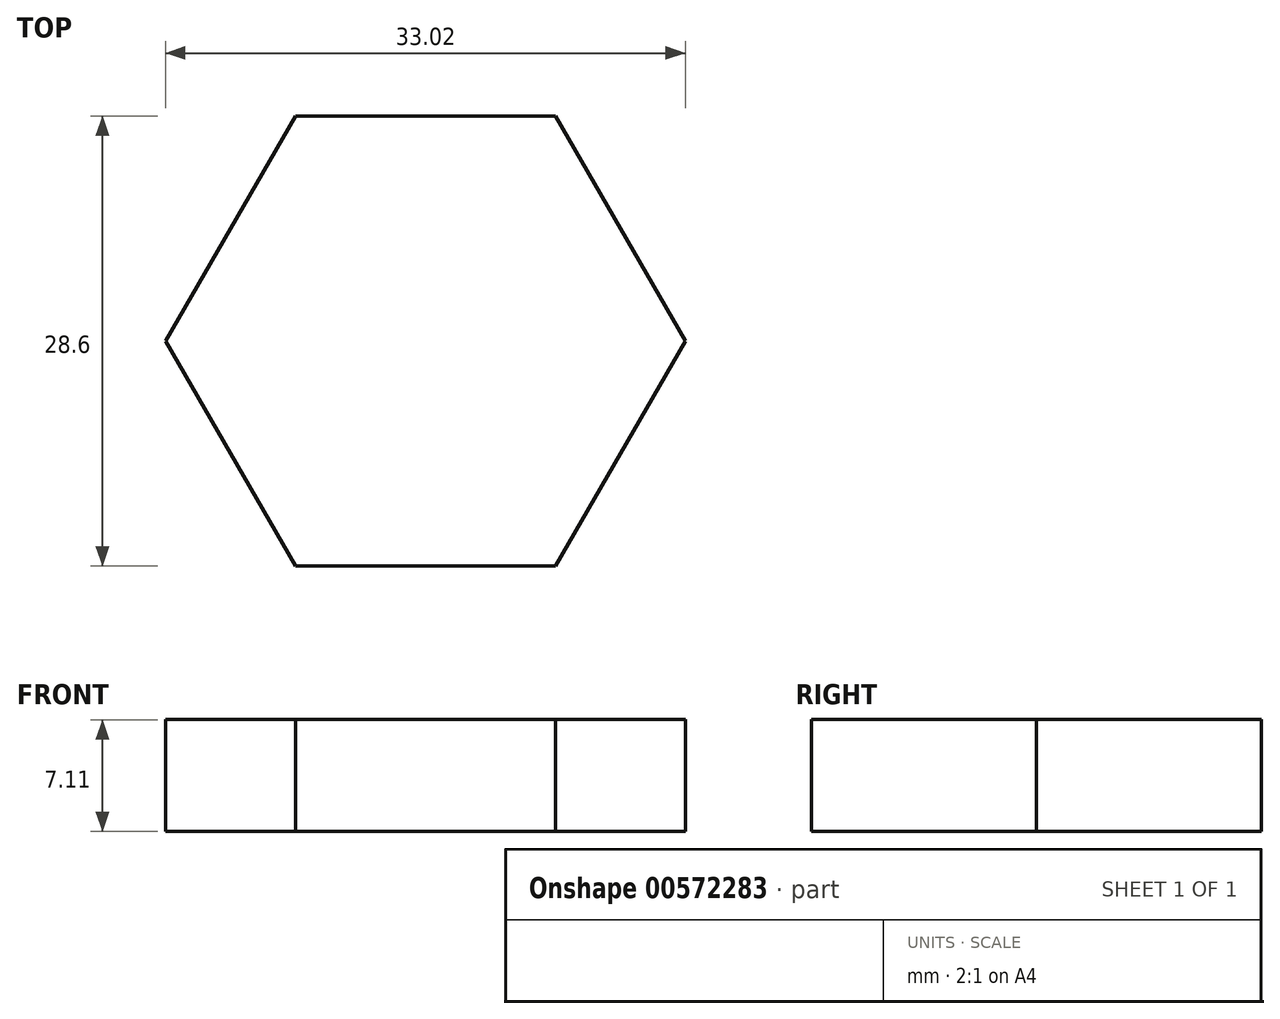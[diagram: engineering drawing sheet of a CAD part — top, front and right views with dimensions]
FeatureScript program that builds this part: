
annotation { "Feature Type Name" : "Feature", "Feature Type Description" : "" }
export const myFeature = defineFeature(function(context is Context, id is Id, definition is map)
    precondition{}
    {
        {
            var Q0;
            Q0=qCreatedBy(makeId("Top.planeOp"),FACE);
            var sketch = newSketch(context, id + "F0", { "sketchPlane" : qUnion([Q0])});
            skCircle(sketch, "E0.cCircle", {"center": v(0, 0) * mm, "radius": 14.3 * mm, "construction": true});
            skLineSegment(sketch, "E0.0", {"start": v(8.26, -14.3) * mm, "end": v(-8.26, -14.3) * mm});
            skLineSegment(sketch, "E0.1", {"start": v(-8.26, -14.3) * mm, "end": v(-16.51, 0) * mm});
            skLineSegment(sketch, "E0.2", {"start": v(-16.51, 0) * mm, "end": v(-8.26, 14.3) * mm});
            skLineSegment(sketch, "E0.3", {"start": v(-8.26, 14.3) * mm, "end": v(8.25, 14.3) * mm});
            skLineSegment(sketch, "E0.4", {"start": v(8.25, 14.3) * mm, "end": v(16.51, 0) * mm});
            skLineSegment(sketch, "E0.5", {"start": v(16.51, 0) * mm, "end": v(8.26, -14.3) * mm});
            skPoint(sketch, "E0.0.midPoint", {"position": v(0, -14.3) * mm});
            skSolve(sketch);
        }
        {
            var Q0;
            Q0 = qSketchRegion(id + "F0", true);
            extrude(context, id + "F1", {"entities" : qUnion([Q0]), "depth" : 7.11 * mm, "offsetDistance" : 25.4 * mm});
        }
        {
            var Q0;
            Q0=qCreatedBy(makeId("Top.planeOp"),FACE);
            var sketch = newSketch(context, id + "F2", { "sketchPlane" : qUnion([Q0])});
            skLineSegment(sketch, "E1", {"start": v(-11.66, -9.07) * mm, "end": v(-5.74, -21.62) * mm});
            skLineSegment(sketch, "E2.MirrorCS", {"start": v(11.66, -9.07) * mm, "end": v(5.74, -21.62) * mm});
            skPoint(sketch, "E3.visualSharp", {"position": v(0, -33.82) * mm});
            skArc(sketch, "E3.filletArc", {"start": v(-5.74, -21.62) * mm, "mid": v(0, -25.26) * mm, "end": v(5.74, -21.62) * mm});
            skLineSegment(sketch, "E4.MirrorCS", {"start": v(11.66, 9.07) * mm, "end": v(5.74, 21.62) * mm});
            skArc(sketch, "E5.MirrorCS", {"start": v(-5.74, 21.62) * mm, "mid": v(0, 25.26) * mm, "end": v(5.74, 21.62) * mm});
            skLineSegment(sketch, "E6.MirrorCS", {"start": v(-11.66, 9.07) * mm, "end": v(-5.74, 21.62) * mm});
            skSolve(sketch);
        }
        {
            var Q0;
            Q0=sQuery(id+"F2.wireOp",EDGE,"E3.filletArc");
            var Q1;
            Q1=sQuery(id+"F2.wireOp",EDGE,"E2.MirrorCS");
            var Q2;
            Q2=sQuery(id+"F2.wireOp",EDGE,"E1");
            var Q3;
            Q3=sQuery(id+"F2.wireOp",EDGE,"E6.MirrorCS");
            var Q4;
            Q4=sQuery(id+"F2.wireOp",EDGE,"E5.MirrorCS");
            var Q5;
            Q5=sQuery(id+"F2.wireOp",EDGE,"E4.MirrorCS");
            extrude(context, id + "F3", {"bodyType" : ToolBodyType.SURFACE, "surfaceEntities" : qUnion([Q0, Q1, Q2, Q3, Q4, Q5]), "depth" : 12.7 * mm, "offsetDistance" : 25.4 * mm});
        }
        {
            var Q0;
            Q0=qCreatedBy(makeId("Top.planeOp"),FACE);
            var sketch = newSketch(context, id + "F4", { "sketchPlane" : qUnion([Q0])});
            skLineSegment(sketch, "E7", {"start": v(11.37, -9.35) * mm, "end": v(19.23, -6.31) * mm});
            skLineSegment(sketch, "E8", {"start": v(18.97, 5.62) * mm, "end": v(11.37, 8.2) * mm});
            skLineSegment(sketch, "E9.MirrorCS", {"start": v(-11.37, -9.35) * mm, "end": v(-19.23, -6.31) * mm});
            skLineSegment(sketch, "E10.MirrorCS", {"start": v(-18.97, 5.62) * mm, "end": v(-11.37, 8.2) * mm});
            skPoint(sketch, "E11.visualSharp", {"position": v(-35.54, 0) * mm});
            skArc(sketch, "E11.filletArc", {"start": v(-18.97, 5.62) * mm, "mid": v(-23.28, -0.26) * mm, "end": v(-19.23, -6.31) * mm});
            skPoint(sketch, "E12.visualSharp", {"position": v(35.54, 0) * mm});
            skArc(sketch, "E12.filletArc", {"start": v(19.23, -6.31) * mm, "mid": v(23.28, -0.26) * mm, "end": v(18.97, 5.62) * mm});
            skSolve(sketch);
        }
        {
            var Q0;
            Q0=sQuery(id+"F4.wireOp",EDGE,"E10.MirrorCS");
            var Q1;
            Q1=sQuery(id+"F4.wireOp",EDGE,"E11.filletArc");
            var Q2;
            Q2=sQuery(id+"F4.wireOp",EDGE,"E9.MirrorCS");
            var Q3;
            Q3=sQuery(id+"F4.wireOp",EDGE,"E7");
            var Q4;
            Q4=sQuery(id+"F4.wireOp",EDGE,"E12.filletArc");
            var Q5;
            Q5=sQuery(id+"F4.wireOp",EDGE,"E8");
            extrude(context, id + "F5", {"bodyType" : ToolBodyType.SURFACE, "surfaceEntities" : qUnion([Q0, Q1, Q2, Q3, Q4, Q5]), "depth" : 12.7 * mm, "offsetDistance" : 25.4 * mm});
        }
    });
